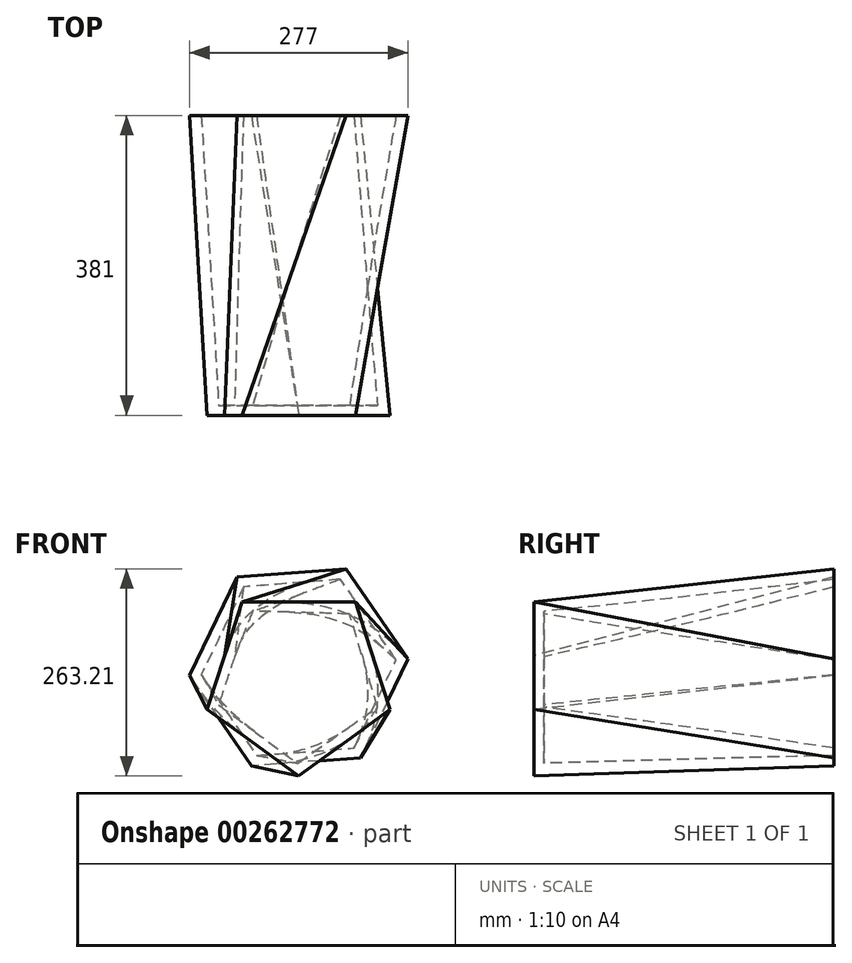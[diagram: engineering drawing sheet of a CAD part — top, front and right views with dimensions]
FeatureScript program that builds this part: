
annotation { "Feature Type Name" : "Feature", "Feature Type Description" : "" }
export const myFeature = defineFeature(function(context is Context, id is Id, definition is map)
    precondition{}
    {
        {
            var Q0;
            Q0=qCreatedBy(makeId("Front.planeOp"),FACE);
            var sketch = newSketch(context, id + "F0", { "sketchPlane" : qUnion([Q0])});
            skCircle(sketch, "E0.cCircle", {"center": v(0, 0) * mm, "radius": 138.9 * mm, "construction": true});
            skLineSegment(sketch, "E0.0", {"start": v(78.3, -114.72) * mm, "end": v(-60.2, -125.17) * mm});
            skLineSegment(sketch, "E0.1", {"start": v(-60.2, -125.17) * mm, "end": v(-138.5, -10.45) * mm});
            skLineSegment(sketch, "E0.2", {"start": v(-138.5, -10.45) * mm, "end": v(-78.3, 114.72) * mm});
            skLineSegment(sketch, "E0.3", {"start": v(-78.3, 114.72) * mm, "end": v(60.2, 125.17) * mm});
            skLineSegment(sketch, "E0.4", {"start": v(60.2, 125.17) * mm, "end": v(138.5, 10.45) * mm});
            skLineSegment(sketch, "E0.5", {"start": v(138.5, 10.45) * mm, "end": v(78.3, -114.72) * mm});
            skSolve(sketch);
        }
        {
            var Q0;
            Q0=makeQuery(id+"F0.imprint","IMPRINT",FACE,{"disambiguationData":[TD([[makeQuery(id+"F0.imprint","IMPRINT",EDGE,{"derivedFrom":sQuery(id+"F0.wireOp",EDGE,"E0.0")}),-1.0]])]});
            cPlane(context, id + "F1", {"entities" : qUnion([Q0]), "cplaneType" : CPlaneType.OFFSET, "offset" : 381 * mm, "width" : 152.4 * mm, "height" : 152.4 * mm});
        }
        {
            var Q0;
            Q0=qCreatedBy(id+"F1.planeOp",FACE);
            var sketch = newSketch(context, id + "F2", { "sketchPlane" : qUnion([Q0])});
            skCircle(sketch, "E1.cCircle", {"center": v(0, -15.9) * mm, "radius": 122.15 * mm, "construction": true});
            skLineSegment(sketch, "E1.0", {"start": v(0, -138.04) * mm, "end": v(-116.17, -53.64) * mm});
            skLineSegment(sketch, "E1.1", {"start": v(-116.17, -53.64) * mm, "end": v(-71.8, 82.92) * mm});
            skLineSegment(sketch, "E1.2", {"start": v(-71.8, 82.92) * mm, "end": v(71.8, 82.92) * mm});
            skLineSegment(sketch, "E1.3", {"start": v(71.8, 82.92) * mm, "end": v(116.17, -53.64) * mm});
            skLineSegment(sketch, "E1.4", {"start": v(116.17, -53.64) * mm, "end": v(0, -138.04) * mm});
            skSolve(sketch);
        }
        {
            var Q0;
            Q0=makeQuery(id+"F0.imprint","IMPRINT",FACE,{"disambiguationData":[TD([[makeQuery(id+"F0.imprint","IMPRINT",EDGE,{"derivedFrom":sQuery(id+"F0.wireOp",EDGE,"E0.0")}),-1.0]])]});
            var Q1;
            Q1=makeQuery(id+"F2.imprint","IMPRINT",FACE,{"disambiguationData":[TD([[makeQuery(id+"F2.imprint","IMPRINT",EDGE,{"derivedFrom":sQuery(id+"F2.wireOp",EDGE,"E1.0")}),-1.0]])]});
            loft(context, id + "F3", {"sheetProfilesArray" : [{ "sheetProfileEntities" : qUnion([Q0]) }, { "sheetProfileEntities" : qUnion([Q1]) }]});
        }
        {
            var Q0;
            Q0=makeQuery(id+"F3.opLoft","CAP_FACE",FACE,{"disambiguationData":[OSD([makeQuery(id+"F0.imprint","IMPRINT",FACE,{"disambiguationData":[TD([[makeQuery(id+"F0.imprint","IMPRINT",EDGE,{"derivedFrom":sQuery(id+"F0.wireOp",EDGE,"E0.0")}),-1.0]])]})])],"isStart":true});
            shell(context, id + "F4", {"entities" : qUnion([Q0]), "thickness" : 12.7 * mm});
        }
    });
